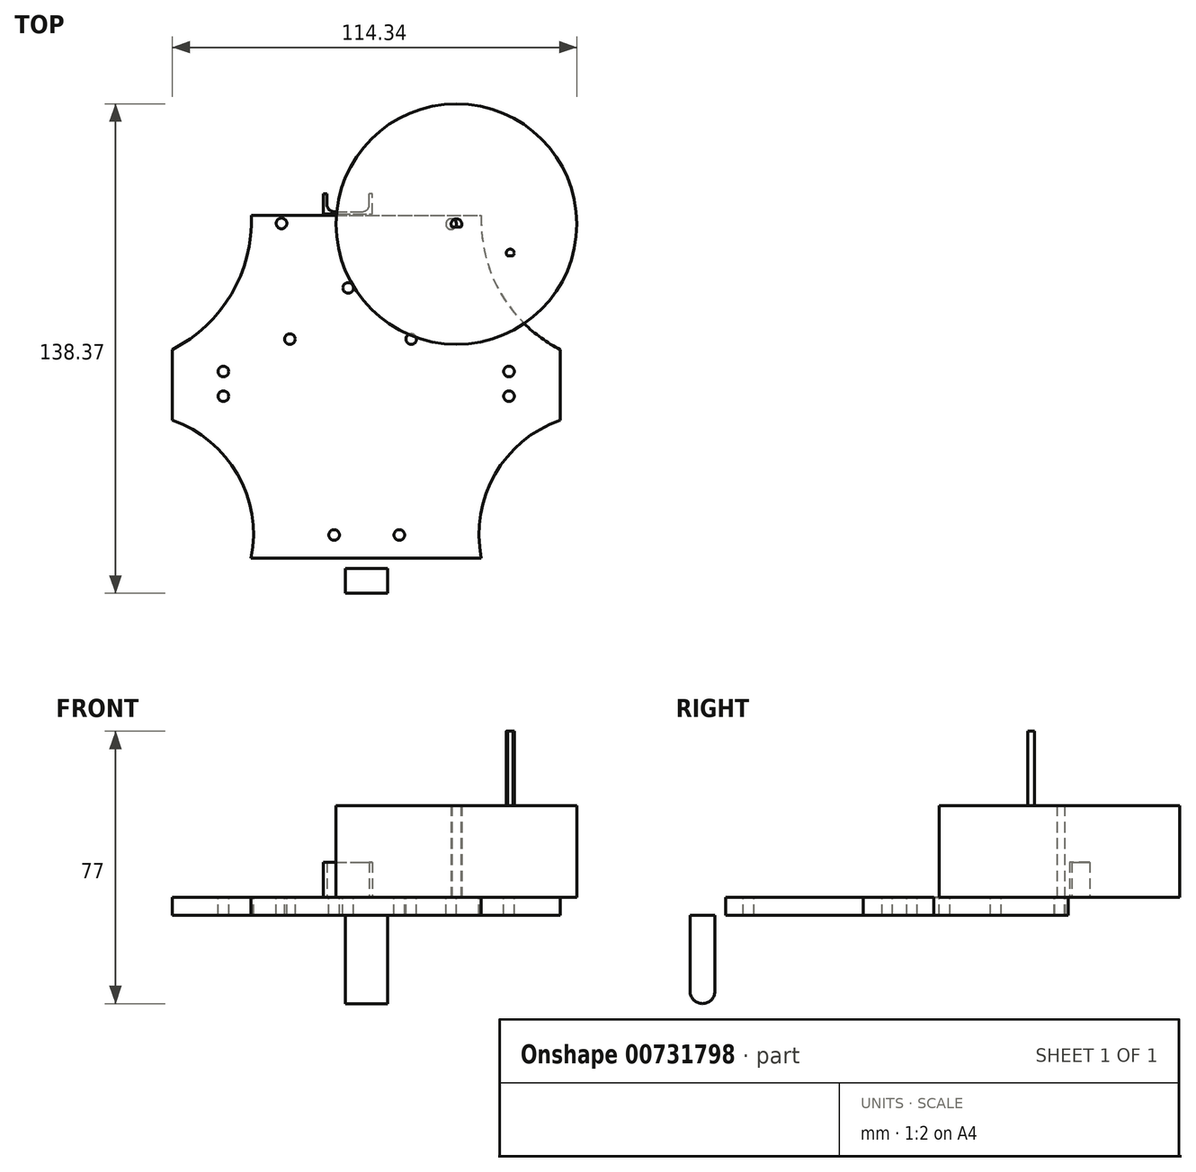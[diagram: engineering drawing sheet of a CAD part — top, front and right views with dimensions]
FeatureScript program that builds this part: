
annotation { "Feature Type Name" : "Feature", "Feature Type Description" : "" }
export const myFeature = defineFeature(function(context is Context, id is Id, definition is map)
    precondition{}
    {
        {
            var Q0;
            Q0=qCreatedBy(makeId("Top.planeOp"),FACE);
            var sketch = newSketch(context, id + "F0", { "sketchPlane" : qUnion([Q0])});
            skCircle(sketch, "E0", {"center": v(0, 0) * mm, "radius": 34 * mm});
            skArc(sketch, "E1", {"start": v(1.29, -0.77) * mm, "mid": v(0, 1.5) * mm, "end": v(-1.29, -0.77) * mm});
            skLineSegment(sketch, "E2", {"start": v(-1.29, -0.77) * mm, "end": v(1.29, -0.77) * mm});
            skSolve(sketch);
        }
        {
            var Q0;
            Q0=makeQuery(id+"F0.imprint","IMPRINT",FACE,{"disambiguationData":[TD([[makeQuery(id+"F0.imprint","IMPRINT",EDGE,{"derivedFrom":sQuery(id+"F0.wireOp",EDGE,"E0")}),1.0]])]});
            extrude(context, id + "F1", {"entities" : qUnion([Q0]), "depth" : 26 * mm, "offsetDistance" : 25 * mm});
        }
        {
            var Q0;
            Q0 = qSketchRegion(id + "F0", true);
            extrude(context, id + "F2", {"entities" : qUnion([Q0]), "operationType" : NewBodyOperationType.ADD, "depth" : 26 * mm, "offsetDistance" : 25 * mm});
        }
        {
            var Q0;
            Q0=qCreatedBy(makeId("Top.planeOp"),FACE);
            var sketch = newSketch(context, id + "F3", { "sketchPlane" : qUnion([Q0])});
            skLineSegment(sketch, "E3.bottom", {"start": v(10.19, -4.7) * mm, "end": v(20.19, -4.7) * mm});
            skLineSegment(sketch, "E3.top", {"start": v(10.19, -11.7) * mm, "end": v(20.19, -11.7) * mm});
            skLineSegment(sketch, "E3.left", {"start": v(10.19, -4.7) * mm, "end": v(10.19, -11.7) * mm});
            skLineSegment(sketch, "E3.right", {"start": v(20.19, -4.7) * mm, "end": v(20.19, -11.7) * mm});
            skArc(sketch, "E4", {"start": v(20.19, -4.7) * mm, "mid": v(15.19, -1.68) * mm, "end": v(10.19, -4.7) * mm});
            skPoint(sketch, "E5.startSnap0", {"position": v(15.19, -1.68) * mm});
            skLineSegment(sketch, "E6", {"start": v(15.19, -1.68) * mm, "end": v(28.85, -1.68) * mm});
            skArc(sketch, "E7", {"start": v(10.19, -11.7) * mm, "mid": v(15.19, -14.63) * mm, "end": v(20.19, -11.7) * mm});
            skLineSegment(sketch, "E8", {"start": v(15.19, -14.63) * mm, "end": v(26.86, -14.63) * mm});
            skSolve(sketch);
        }
        {
            var Q0;
            {var subQ0=sQuery(id+"F3.wireOp",EDGE,"E3.bottom");Q0=makeQuery(id+"F3.imprint","IMPRINT",FACE,{"disambiguationData":[TD([[makeQuery(id+"F3.imprint","IMPRINT",EDGE,{"derivedFrom":subQ0}),1.0]])]});}
            var Q1;
            {var subQ0=sQuery(id+"F3.wireOp",EDGE,"E3.top");Q1=makeQuery(id+"F3.imprint","IMPRINT",FACE,{"disambiguationData":[TD([[makeQuery(id+"F3.imprint","IMPRINT",EDGE,{"derivedFrom":subQ0}),-1.0]])]});}
            var Q2;
            Q2=makeQuery(id+"F3.imprint","IMPRINT",FACE,{"disambiguationData":[TD([[makeQuery(id+"F3.imprint","IMPRINT",EDGE,{"derivedFrom":sQuery(id+"F3.wireOp",EDGE,"E3.bottom")}),-1.0]])]});
            extrude(context, id + "F4", {"entities" : qUnion([Q0, Q1, Q2]), "depth" : 22 * mm, "offsetDistance" : 25 * mm});
        }
        {
            var Q0;
            Q0=makeQuery(id+"F4.opExtrude","CAP_FACE",FACE,{"disambiguationData":[OSD([sQuery(id+"F3.wireOp",EDGE,"E3.left"),sQuery(id+"F3.wireOp",EDGE,"E3.right"),sQuery(id+"F3.wireOp",EDGE,"E4"),sQuery(id+"F3.wireOp",EDGE,"E7")])],"isStart":false});
            var sketch = newSketch(context, id + "F5", { "sketchPlane" : qUnion([Q0])});
            skArc(sketch, "E9", {"start": v(15.97, -9) * mm, "mid": v(15.19, -7.08) * mm, "end": v(14.41, -9) * mm});
            skPoint(sketch, "E9.centerSnap0", {"position": v(10.19, -8.2) * mm});
            skPoint(sketch, "E9.centerSnap1", {"position": v(15.19, -14.63) * mm});
            skLineSegment(sketch, "E10", {"start": v(14.41, -9) * mm, "end": v(15.97, -9) * mm});
            skSolve(sketch);
        }
        {
            var Q0;
            Q0 = qSketchRegion(id + "F5", true);
            extrude(context, id + "F6", {"entities" : qUnion([Q0]), "operationType" : NewBodyOperationType.ADD, "depth" : 17 * mm, "offsetDistance" : 25 * mm});
        }
        {
            var Q0;
            Q0=qCreatedBy(makeId("Top.planeOp"),FACE);
            var sketch = newSketch(context, id + "F7", { "sketchPlane" : qUnion([Q0])});
            skLineSegment(sketch, "E11.bottom", {"start": v(-57.98, 2.5) * mm, "end": v(7.02, 2.5) * mm});
            skArc(sketch, "E12", {"start": v(7.02, 2.5) * mm, "mid": v(12.62, -19.76) * mm, "end": v(29.34, -35.49) * mm});
            skLineSegment(sketch, "E13", {"start": v(29.34, -35.49) * mm, "end": v(29.34, -55.49) * mm});
            skArc(sketch, "E14", {"start": v(29.34, -55.49) * mm, "mid": v(10.86, -70.73) * mm, "end": v(7.02, -94.37) * mm});
            skLineSegment(sketch, "E15", {"start": v(7.02, -94.37) * mm, "end": v(-57.98, -94.37) * mm});
            skArc(sketch, "E16.MirrorCS", {"start": v(-57.94, 2.5) * mm, "mid": v(-63.58, -19.77) * mm, "end": v(-80.34, -35.48) * mm});
            skArc(sketch, "E17.MirrorCS", {"start": v(-80.34, -55.48) * mm, "mid": v(-61.85, -70.72) * mm, "end": v(-58.02, -94.37) * mm});
            skCircle(sketch, "E18", {"center": v(-16.15, -87.87) * mm, "radius": 1.5 * mm});
            skCircle(sketch, "E19.MirrorC", {"center": v(-34.57, -87.87) * mm, "radius": 1.5 * mm});
            skCircle(sketch, "E20", {"center": v(-1.5, 0) * mm, "radius": 1.5 * mm});
            skCircle(sketch, "E21.MirrorC", {"center": v(-49.42, 0.18) * mm, "radius": 1.5 * mm});
            skCircle(sketch, "E22", {"center": v(-65.84, -48.66) * mm, "radius": 1.5 * mm});
            skCircle(sketch, "E23.MirrorC", {"center": v(-65.84, -41.69) * mm, "radius": 1.5 * mm});
            skCircle(sketch, "E24.MirrorC", {"center": v(14.84, -41.69) * mm, "radius": 1.5 * mm});
            skCircle(sketch, "E25.MirrorC", {"center": v(14.84, -48.66) * mm, "radius": 1.5 * mm});
            skLineSegment(sketch, "E26", {"start": v(-80.34, -35.48) * mm, "end": v(-80.34, -55.48) * mm});
            skLineSegment(sketch, "E27", {"start": v(-57.98, -94.37) * mm, "end": v(-58.02, -94.37) * mm});
            skCircle(sketch, "E28", {"center": v(-12.77, -32.5) * mm, "radius": 1.5 * mm});
            skCircle(sketch, "E29", {"center": v(-47.05, -32.5) * mm, "radius": 1.5 * mm});
            skCircle(sketch, "E30", {"center": v(-30.6, -18.02) * mm, "radius": 1.5 * mm});
            skSolve(sketch);
        }
        {
            var Q0;
            {var subQ1=sQuery(id+"F7.wireOp",EDGE,"E12");Q0=makeQuery(id+"F7.imprint","IMPRINT",FACE,{"disambiguationData":[TD([[makeQuery(id+"F7.imprint","IMPRINT",EDGE,{"derivedFrom":subQ1}),-1.0]])]});}
            extrude(context, id + "F8", {"entities" : qUnion([Q0]), "oppositeDirection" : true, "depth" : 5 * mm, "offsetDistance" : 25 * mm});
        }
        {
            var Q0;
            Q0=makeQuery(id+"F8.opExtrude","CAP_FACE",FACE,{"disambiguationData":[OSD([sQuery(id+"F7.wireOp",EDGE,"E11.bottom"),sQuery(id+"F7.wireOp",EDGE,"E12"),sQuery(id+"F7.wireOp",EDGE,"E13"),sQuery(id+"F7.wireOp",EDGE,"E14"),sQuery(id+"F7.wireOp",EDGE,"E15"),sQuery(id+"F7.wireOp",EDGE,"E16.MirrorCS"),sQuery(id+"F7.wireOp",EDGE,"E17.MirrorCS"),sQuery(id+"F7.wireOp",EDGE,"E18"),sQuery(id+"F7.wireOp",EDGE,"E19.MirrorC"),sQuery(id+"F7.wireOp",EDGE,"E20"),sQuery(id+"F7.wireOp",EDGE,"E21.MirrorC"),sQuery(id+"F7.wireOp",EDGE,"E22"),sQuery(id+"F7.wireOp",EDGE,"E23.MirrorC"),sQuery(id+"F7.wireOp",EDGE,"E24.MirrorC"),sQuery(id+"F7.wireOp",EDGE,"E25.MirrorC"),sQuery(id+"F7.wireOp",EDGE,"E26"),sQuery(id+"F7.wireOp",EDGE,"E27")])],"isStart":false});
            var sketch = newSketch(context, id + "F9", { "sketchPlane" : qUnion([Q0])});
            skLineSegment(sketch, "E31.bottom", {"start": v(-31.45, 104.37) * mm, "end": v(-19.45, 104.37) * mm});
            skLineSegment(sketch, "E31.top", {"start": v(-31.45, 97.37) * mm, "end": v(-19.45, 97.37) * mm});
            skLineSegment(sketch, "E31.left", {"start": v(-31.45, 104.37) * mm, "end": v(-31.45, 97.37) * mm});
            skLineSegment(sketch, "E31.right", {"start": v(-19.45, 104.37) * mm, "end": v(-19.45, 97.37) * mm});
            skSolve(sketch);
        }
        {
            var Q0;
            Q0=makeQuery(id+"F9.imprint","IMPRINT",FACE,{"disambiguationData":[TD([[makeQuery(id+"F9.imprint","IMPRINT",EDGE,{"derivedFrom":sQuery(id+"F9.wireOp",EDGE,"E31.bottom")}),-1.0]])]});
            extrude(context, id + "F10", {"entities" : qUnion([Q0]), "operationType" : NewBodyOperationType.ADD, "depth" : 25 * mm, "offsetDistance" : 25 * mm});
        }
        {
            var Q0;
            Q0=makeQuery(id+"F10.opExtrude","CAP_EDGE",EDGE,{"disambiguationData":[OSD([sQuery(id+"F9.wireOp",EDGE,"E31.bottom")])],"isStart":false});
            var Q1;
            Q1=makeQuery(id+"F10.opExtrude","CAP_EDGE",EDGE,{"disambiguationData":[OSD([sQuery(id+"F9.wireOp",EDGE,"E31.top")])],"isStart":false});
            fillet(context, id + "F11", {"entities" : qUnion([Q0, Q1]), "radius" : 3.5 * mm, "tangentPropagation" : true, "allowEdgeOverflow" : false});
        }
        {
            var Q0;
            Q0 = qSketchRegion(id + "F5", true);
            extrude(context, id + "F12", {"entities" : qUnion([Q0]), "operationType" : NewBodyOperationType.ADD, "depth" : 25 * mm, "offsetDistance" : 25 * mm});
        }
        {
            var Q0;
            Q0=qCreatedBy(makeId("Top.planeOp"),FACE);
            var sketch = newSketch(context, id + "F13", { "sketchPlane" : qUnion([Q0])});
            skLineSegment(sketch, "E32.bottom", {"start": v(-34.61, 3.52) * mm, "end": v(-26.61, 3.52) * mm});
            skLineSegment(sketch, "E32.top", {"start": v(-36.61, 8.52) * mm, "end": v(-24.61, 8.52) * mm});
            skLineSegment(sketch, "E32.left", {"start": v(-36.61, 5.52) * mm, "end": v(-36.61, 8.52) * mm});
            skLineSegment(sketch, "E32.right", {"start": v(-24.61, 5.52) * mm, "end": v(-24.61, 8.52) * mm});
            skPoint(sketch, "E33.visualSharp", {"position": v(-24.61, 3.52) * mm});
            skArc(sketch, "E33.filletArc", {"start": v(-26.61, 3.52) * mm, "mid": v(-25.2, 4.1) * mm, "end": v(-24.61, 5.52) * mm});
            skPoint(sketch, "E34.visualSharp", {"position": v(-36.61, 3.52) * mm});
            skArc(sketch, "E34.filletArc", {"start": v(-36.61, 5.52) * mm, "mid": v(-36.03, 4.1) * mm, "end": v(-34.61, 3.52) * mm});
            skLineSegment(sketch, "E35", {"start": v(-37.59, 8.52) * mm, "end": v(-37.59, 2.87) * mm});
            skLineSegment(sketch, "E36", {"start": v(-37.59, 2.87) * mm, "end": v(-23.7, 2.87) * mm});
            skLineSegment(sketch, "E37", {"start": v(-23.7, 2.87) * mm, "end": v(-23.7, 8.52) * mm});
            skLineSegment(sketch, "E38", {"start": v(-23.7, 8.52) * mm, "end": v(-37.59, 8.52) * mm});
            skLineSegment(sketch, "E39", {"start": v(-23.7, 8.52) * mm, "end": v(-21.9, 8.52) * mm});
            skLineSegment(sketch, "E40", {"start": v(-37.59, 8.52) * mm, "end": v(-39.49, 8.52) * mm});
            skSolve(sketch);
        }
        {
            var Q0;
            Q0=makeQuery(id+"F13.imprint","IMPRINT",FACE,{"disambiguationData":[TD([[makeQuery(id+"F13.imprint","IMPRINT",EDGE,{"derivedFrom":sQuery(id+"F13.wireOp",EDGE,"E32.bottom")}),-1.0]])]});
            extrude(context, id + "F14", {"entities" : qUnion([Q0]), "depth" : 10 * mm, "offsetDistance" : 25 * mm});
        }
    });
